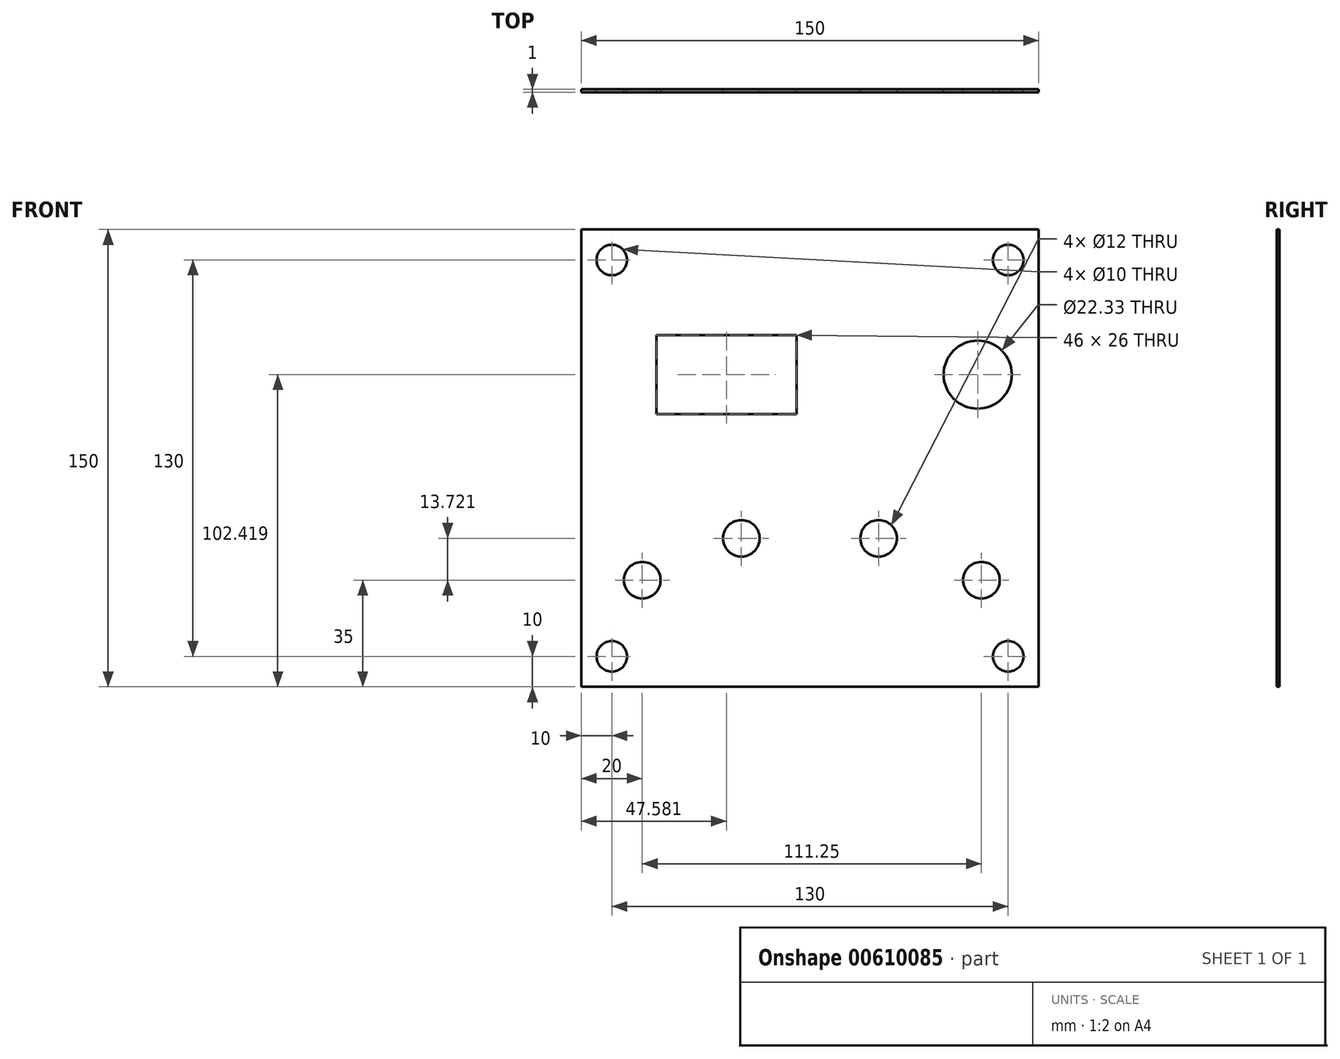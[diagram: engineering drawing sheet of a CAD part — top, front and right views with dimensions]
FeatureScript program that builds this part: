
annotation { "Feature Type Name" : "Feature", "Feature Type Description" : "" }
export const myFeature = defineFeature(function(context is Context, id is Id, definition is map)
    precondition{}
    {
        {
            var Q0;
            Q0=qCreatedBy(makeId("Front.planeOp"),FACE);
            var sketch = newSketch(context, id + "F0", { "sketchPlane" : qUnion([Q0])});
            skLineSegment(sketch, "E0.bottom", {"start": v(75, 75) * mm, "end": v(-75, 75) * mm});
            skLineSegment(sketch, "E0.top", {"start": v(75, -75) * mm, "end": v(-75, -75) * mm});
            skLineSegment(sketch, "E0.left", {"start": v(75, 75) * mm, "end": v(75, -75) * mm});
            skLineSegment(sketch, "E0.right", {"start": v(-75, 75) * mm, "end": v(-75, -75) * mm});
            skPoint(sketch, "E0.middle", {"position": v(0, 0) * mm});
            skLineSegment(sketch, "E1.left", {"start": v(75, -75) * mm, "end": v(75, -75) * mm});
            skLineSegment(sketch, "E1.right", {"start": v(-75, -75) * mm, "end": v(-75, -75) * mm});
            skPoint(sketch, "E1.middle", {"position": v(0, -75) * mm});
            skPoint(sketch, "E2.endSnap0", {"position": v(0, 75) * mm});
            skCircle(sketch, "E3", {"center": v(-65, 65) * mm, "radius": 5 * mm});
            skCircle(sketch, "E4.MirrorC", {"center": v(65, 65) * mm, "radius": 5 * mm});
            skCircle(sketch, "E5.MirrorC", {"center": v(65, -65) * mm, "radius": 5 * mm});
            skCircle(sketch, "E6.MirrorC", {"center": v(-65, -65) * mm, "radius": 5 * mm});
            skPoint(sketch, "E7.middle", {"position": v(0, 40) * mm});
            skPoint(sketch, "E8.middle", {"position": v(0, -15) * mm});
            skLineSegment(sketch, "E9", {"start": v(-75, 0) * mm, "end": v(-75, 15) * mm});
            skCircle(sketch, "E10", {"center": v(56.25, -40) * mm, "radius": 6 * mm});
            skCircle(sketch, "E11", {"center": v(55, 27.42) * mm, "radius": 11.17 * mm});
            skPoint(sketch, "E11.centerSnap0", {"position": v(55, 30.76) * mm});
            skLineSegment(sketch, "E12.bottom", {"start": v(-50.42, 40.42) * mm, "end": v(-4.42, 40.42) * mm});
            skLineSegment(sketch, "E12.top", {"start": v(-50.42, 14.42) * mm, "end": v(-4.42, 14.42) * mm});
            skLineSegment(sketch, "E12.left", {"start": v(-50.42, 40.42) * mm, "end": v(-50.42, 14.42) * mm});
            skLineSegment(sketch, "E12.right", {"start": v(-4.42, 40.42) * mm, "end": v(-4.42, 14.42) * mm});
            skPoint(sketch, "E12.middle", {"position": v(-27.42, 27.42) * mm});
            skCircle(sketch, "E13", {"center": v(-55, -40) * mm, "radius": 6 * mm});
            skCircle(sketch, "E14", {"center": v(-22.51, -26.28) * mm, "radius": 6 * mm});
            skCircle(sketch, "E15.MirrorC", {"center": v(22.51, -26.28) * mm, "radius": 6 * mm});
            skSolve(sketch);
        }
        {
            var Q0;
            {var subQ2=sQuery(id+"F0.wireOp",EDGE,"E0.bottom");Q0=makeQuery(id+"F0.imprint","IMPRINT",FACE,{"disambiguationData":[TD([[makeQuery(id+"F0.imprint","IMPRINT",EDGE,{"derivedFrom":subQ2}),1.0]])]});}
            extrude(context, id + "F1", {"entities" : qUnion([Q0]), "depth" : 1 * mm, "offsetDistance" : 25 * mm});
        }
    });
